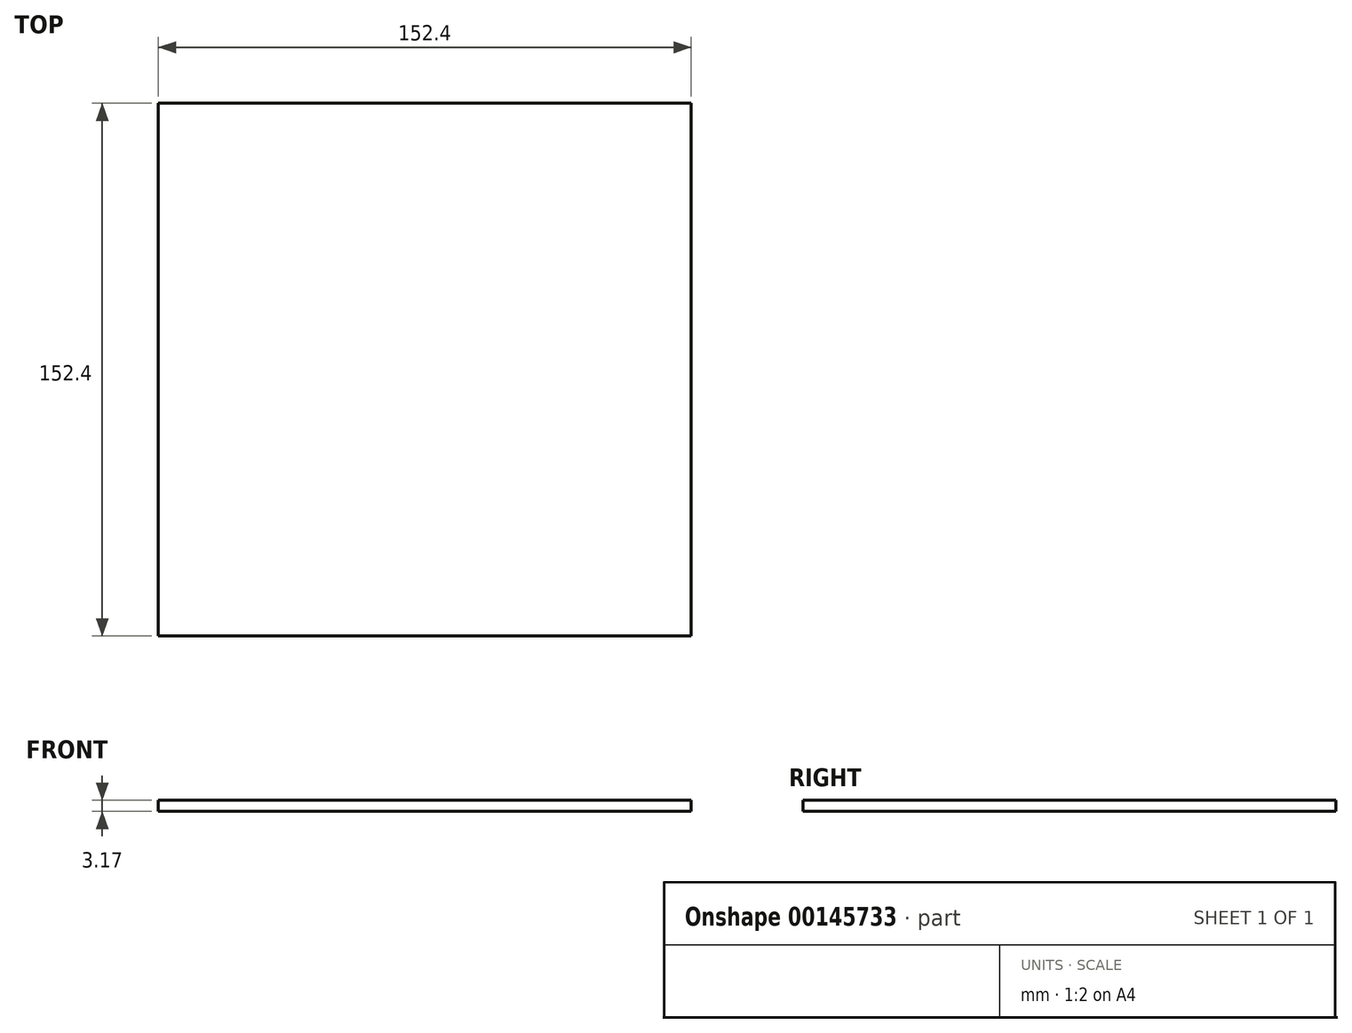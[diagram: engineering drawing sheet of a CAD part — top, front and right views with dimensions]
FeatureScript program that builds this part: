
annotation { "Feature Type Name" : "Feature", "Feature Type Description" : "" }
export const myFeature = defineFeature(function(context is Context, id is Id, definition is map)
    precondition{}
    {
        {
            var Q0;
            Q0=qCreatedBy(makeId("Top.planeOp"),FACE);
            var sketch = newSketch(context, id + "F0", { "sketchPlane" : qUnion([Q0])});
            skLineSegment(sketch, "E0.bottom", {"start": v(79.32, 76.2) * mm, "end": v(-73.08, 76.2) * mm});
            skLineSegment(sketch, "E0.top", {"start": v(79.32, -76.2) * mm, "end": v(-73.08, -76.2) * mm});
            skLineSegment(sketch, "E0.left", {"start": v(79.32, 76.2) * mm, "end": v(79.32, -76.2) * mm});
            skLineSegment(sketch, "E0.right", {"start": v(-73.08, 76.2) * mm, "end": v(-73.08, -76.2) * mm});
            skPoint(sketch, "E0.middle", {"position": v(3.12, 0) * mm});
            skSolve(sketch);
        }
        {
            var Q0;
            Q0 = qSketchRegion(id + "F0", true);
            extrude(context, id + "F1", {"entities" : qUnion([Q0]), "depth" : 3.17 * mm});
        }
    });
